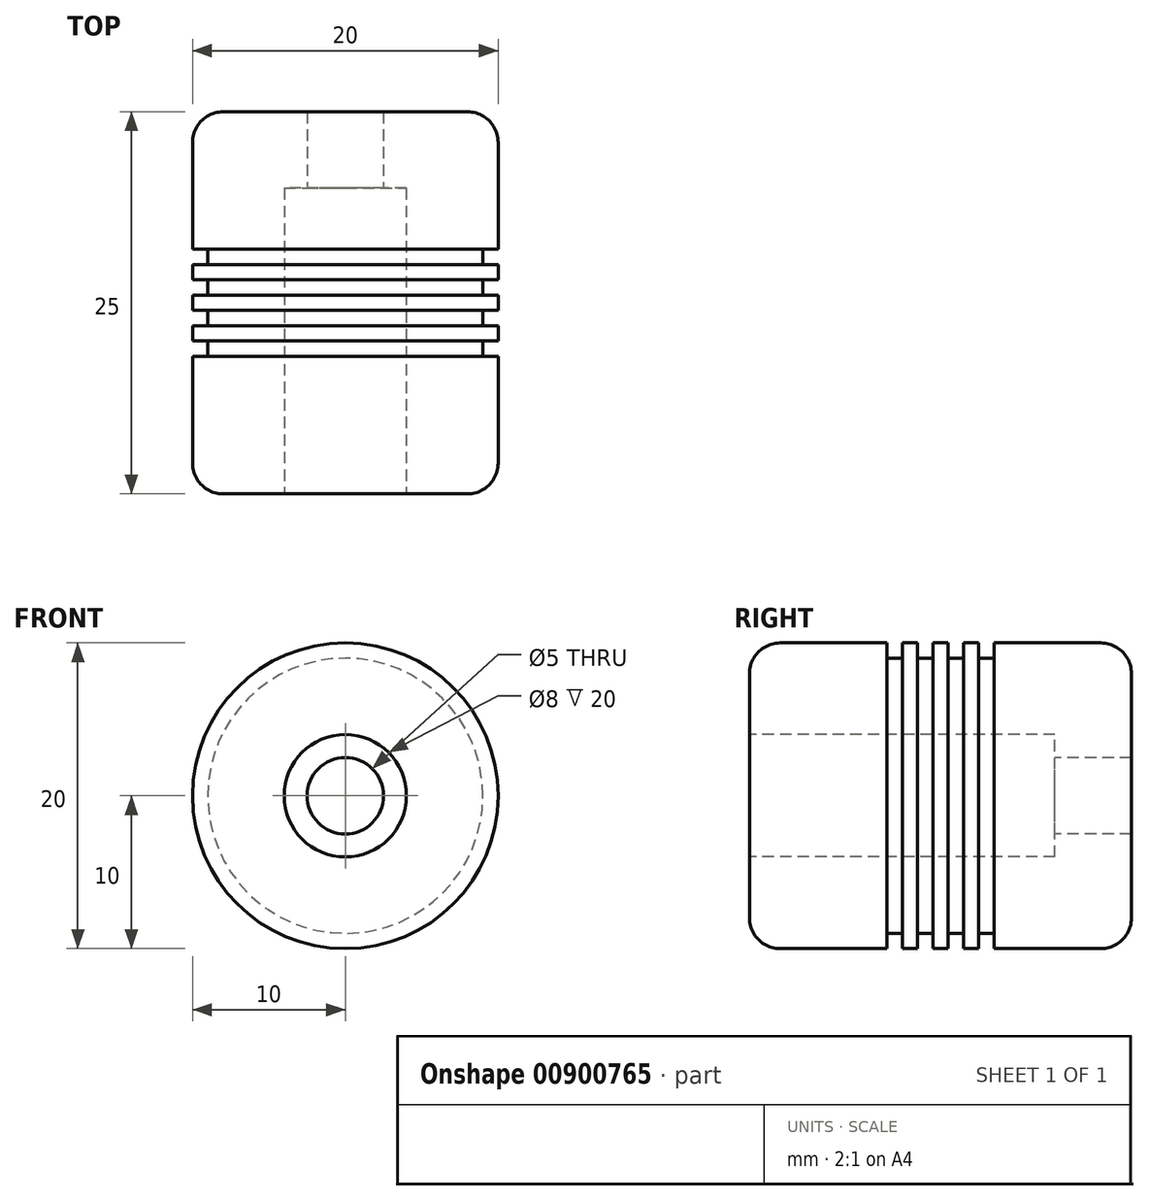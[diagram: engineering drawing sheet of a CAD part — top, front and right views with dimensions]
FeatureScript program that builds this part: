
annotation { "Feature Type Name" : "Feature", "Feature Type Description" : "" }
export const myFeature = defineFeature(function(context is Context, id is Id, definition is map)
    precondition{}
    {
        {
            var Q0;
            Q0=qCreatedBy(makeId("Front.planeOp"),FACE);
            var sketch = newSketch(context, id + "F0", { "sketchPlane" : qUnion([Q0])});
            skCircle(sketch, "E0", {"center": v(0, 0) * mm, "radius": 2.5 * mm});
            skCircle(sketch, "E1", {"center": v(0, 0) * mm, "radius": 10 * mm});
            skSolve(sketch);
        }
        {
            var Q0;
            Q0 = qSketchRegion(id + "F0", true);
            extrude(context, id + "F1", {"entities" : qUnion([Q0]), "oppositeDirection" : true, "depth" : 25 * mm, "offsetDistance" : 25 * mm});
        }
        {
            var Q0;
            Q0=qCreatedBy(makeId("Right.planeOp"),FACE);
            var sketch = newSketch(context, id + "F2", { "sketchPlane" : qUnion([Q0])});
            skLineSegment(sketch, "E2", {"start": v(12.5, 10) * mm, "end": v(12.5, -10) * mm, "construction": true});
            skLineSegment(sketch, "E3", {"start": v(0, 10) * mm, "end": v(25, 10) * mm, "construction": true});
            skLineSegment(sketch, "E4", {"start": v(25, -10) * mm, "end": v(0, -10) * mm, "construction": true});
            skLineSegment(sketch, "E5.bottom", {"start": v(9, 10) * mm, "end": v(10, 10) * mm});
            skLineSegment(sketch, "E5.top", {"start": v(9, 9) * mm, "end": v(10, 9) * mm});
            skLineSegment(sketch, "E5.left", {"start": v(9, 10) * mm, "end": v(9, 9) * mm});
            skLineSegment(sketch, "E5.right", {"start": v(10, 10) * mm, "end": v(10, 9) * mm});
            skLineSegment(sketch, "E6.1.0.0", {"start": v(11, 9) * mm, "end": v(12, 9) * mm});
            skLineSegment(sketch, "E6.1.0.1", {"start": v(11, 10) * mm, "end": v(11, 9) * mm});
            skLineSegment(sketch, "E6.1.0.2", {"start": v(12, 10) * mm, "end": v(12, 9) * mm});
            skLineSegment(sketch, "E6.1.0.3", {"start": v(11, 10) * mm, "end": v(12, 10) * mm});
            skLineSegment(sketch, "E6.2.0.0", {"start": v(13, 9) * mm, "end": v(14, 9) * mm});
            skLineSegment(sketch, "E6.2.0.1", {"start": v(13, 10) * mm, "end": v(13, 9) * mm});
            skLineSegment(sketch, "E6.2.0.2", {"start": v(14, 10) * mm, "end": v(14, 9) * mm});
            skLineSegment(sketch, "E6.2.0.3", {"start": v(13, 10) * mm, "end": v(14, 10) * mm});
            skLineSegment(sketch, "E6.3.0.0", {"start": v(15, 9) * mm, "end": v(16, 9) * mm});
            skLineSegment(sketch, "E6.3.0.1", {"start": v(15, 10) * mm, "end": v(15, 9) * mm});
            skLineSegment(sketch, "E6.3.0.2", {"start": v(16, 10) * mm, "end": v(16, 9) * mm});
            skLineSegment(sketch, "E6.3.0.3", {"start": v(15, 10) * mm, "end": v(16, 10) * mm});
            skLineSegment(sketch, "E6.direction1", {"start": v(9, 9) * mm, "end": v(11, 9) * mm});
            skLineSegment(sketch, "E7", {"start": v(12, 9) * mm, "end": v(13, 9) * mm, "construction": true});
            skPoint(sketch, "E8", {"position": v(12.5, 9) * mm});
            skSolve(sketch);
        }
        {
            var Q0;
            Q0 = qSketchRegion(id + "F2", true);
            var Q1;
            Q1=makeQuery(id+"F1.opExtrude","CAP_EDGE",EDGE,{"disambiguationData":[OSD([sQuery(id+"F0.wireOp",EDGE,"E0")])],"isStart":false});
            revolve(context, id + "F3", {"operationType" : NewBodyOperationType.REMOVE, "surfaceOperationType" : NewSurfaceOperationType.NEW, "entities" : qUnion([Q0]), "axis" : qUnion([Q1]), "revolveType" : RevolveType.FULL});
        }
        {
            var Q0;
            Q0=makeQuery(id+"F1.opExtrude","CAP_EDGE",EDGE,{"disambiguationData":[OSD([sQuery(id+"F0.wireOp",EDGE,"E1")])],"isStart":true});
            var Q1;
            Q1=makeQuery(id+"F1.opExtrude","CAP_EDGE",EDGE,{"disambiguationData":[OSD([sQuery(id+"F0.wireOp",EDGE,"E1")])],"isStart":false});
            fillet(context, id + "F4", {"entities" : qUnion([Q0, Q1]), "radius" : 2 * mm, "tangentPropagation" : true, "allowEdgeOverflow" : false});
        }
        {
            var Q0;
            Q0=makeQuery(id+"F1.opExtrude","CAP_FACE",FACE,{"disambiguationData":[OSD([sQuery(id+"F0.wireOp",EDGE,"E0"),sQuery(id+"F0.wireOp",EDGE,"E1")])],"isStart":true});
            var sketch = newSketch(context, id + "F5", { "sketchPlane" : qUnion([Q0])});
            skCircle(sketch, "E9", {"center": v(0, 0) * mm, "radius": 4 * mm});
            skSolve(sketch);
        }
        {
            var Q0;
            Q0 = qSketchRegion(id + "F5", true);
            extrude(context, id + "F6", {"entities" : qUnion([Q0]), "operationType" : NewBodyOperationType.REMOVE, "oppositeDirection" : true, "depth" : 20 * mm, "offsetDistance" : 25 * mm});
        }
    });
